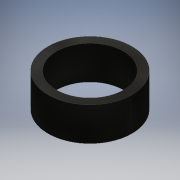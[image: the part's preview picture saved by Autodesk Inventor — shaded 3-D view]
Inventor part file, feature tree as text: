
AUTODESK INVENTOR PART (.ipt)
format: ipt  version: 2016 (Build 200138000, 138)  size: 96,768 bytes
history: native  units: mm
features: other x1, extrude x1, sketch x1
ambient origin geometry x8: Origin, YZ Plane, XZ Plane, XY Plane, X Axis, Y Axis, Z Axis, Center Point
bodies: Body1 (feature_tree)
feature tree (3):
  other  "ソリッド1"
  extrude  "押し出し1"  Depth=8.0mm
  sketch  "スケッチ1"
